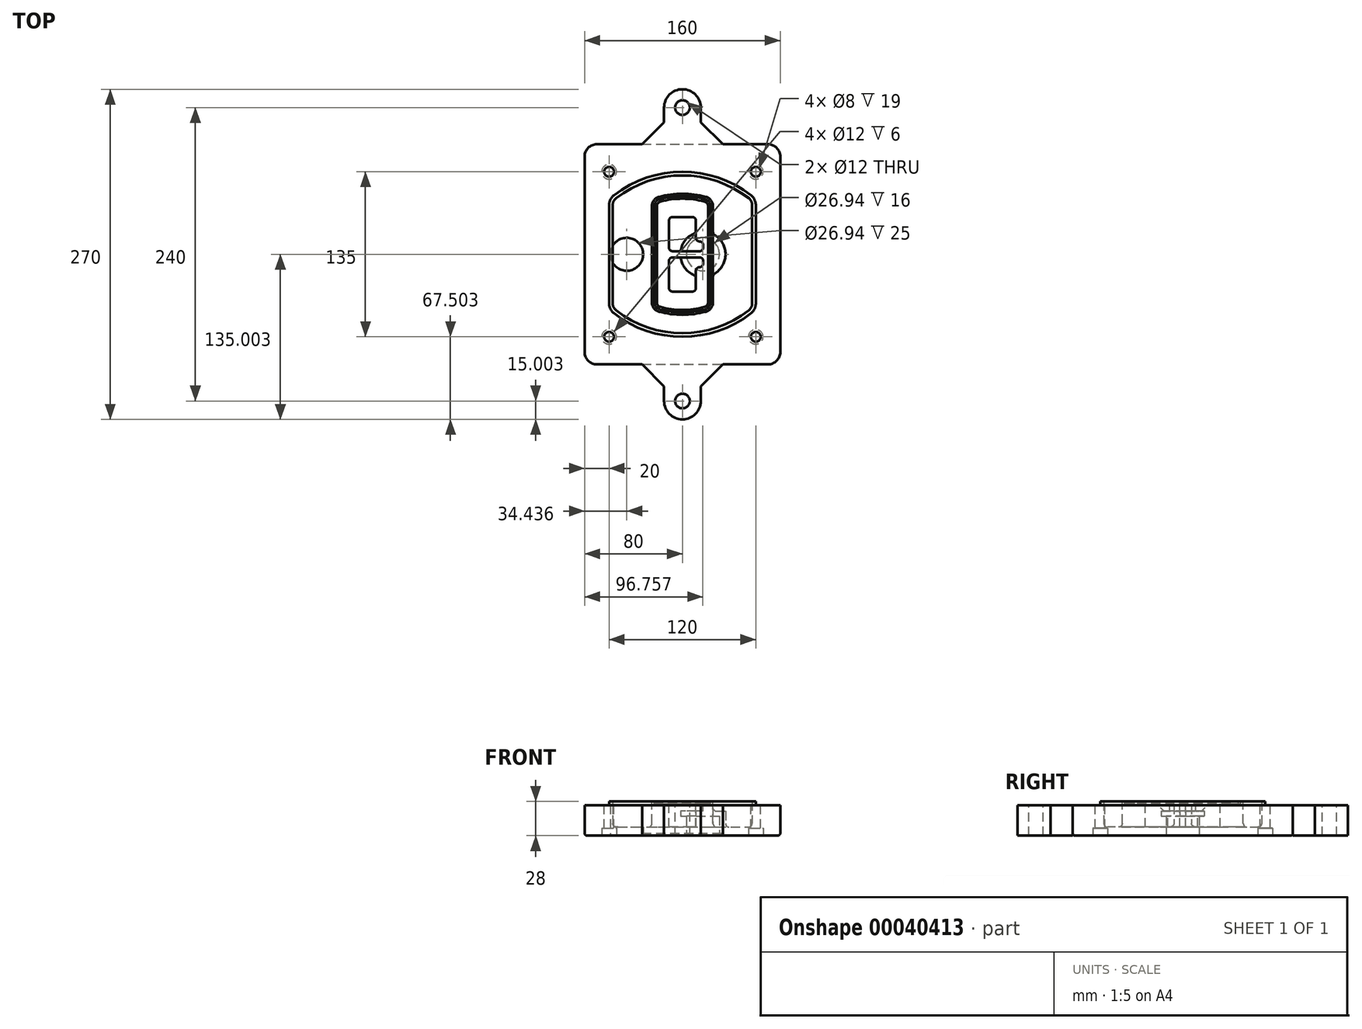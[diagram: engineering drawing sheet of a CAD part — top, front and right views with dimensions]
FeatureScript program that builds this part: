
annotation { "Feature Type Name" : "Feature", "Feature Type Description" : "" }
export const myFeature = defineFeature(function(context is Context, id is Id, definition is map)
    precondition{}
    {
        {
            var Q0;
            Q0=qCreatedBy(makeId("Top.planeOp"),FACE);
            var sketch = newSketch(context, id + "F0", { "sketchPlane" : qUnion([Q0])});
            skPoint(sketch, "E0.rect.middle", {"position": v(0, 0) * mm});
            skLineSegment(sketch, "E1.bottom", {"start": v(24.05, 28.38) * mm, "end": v(164.05, 28.38) * mm});
            skLineSegment(sketch, "E1.top", {"start": v(24.05, 208.38) * mm, "end": v(164.05, 208.38) * mm});
            skLineSegment(sketch, "E1.left", {"start": v(14.05, 38.38) * mm, "end": v(14.05, 198.38) * mm});
            skLineSegment(sketch, "E1.right", {"start": v(174.05, 38.38) * mm, "end": v(174.05, 198.38) * mm});
            skLineSegment(sketch, "E2", {"start": v(14.05, 208.38) * mm, "end": v(174.05, 28.38) * mm, "construction": true});
            skLineSegment(sketch, "E3", {"start": v(174.05, 208.38) * mm, "end": v(14.05, 28.38) * mm, "construction": true});
            skCircle(sketch, "E4", {"center": v(34.05, 185.88) * mm, "radius": 4 * mm});
            skCircle(sketch, "E5", {"center": v(154.05, 185.88) * mm, "radius": 4 * mm});
            skCircle(sketch, "E6", {"center": v(154.05, 50.88) * mm, "radius": 4 * mm});
            skCircle(sketch, "E7", {"center": v(34.05, 50.88) * mm, "radius": 4 * mm});
            skLineSegment(sketch, "E8", {"start": v(34.05, 185.88) * mm, "end": v(154.05, 185.88) * mm, "construction": true});
            skLineSegment(sketch, "E9", {"start": v(154.05, 185.88) * mm, "end": v(154.05, 50.88) * mm, "construction": true});
            skLineSegment(sketch, "E10", {"start": v(154.05, 50.88) * mm, "end": v(34.05, 50.88) * mm, "construction": true});
            skLineSegment(sketch, "E11", {"start": v(34.05, 50.88) * mm, "end": v(34.05, 185.88) * mm, "construction": true});
            skLineSegment(sketch, "E12", {"start": v(34.05, 158.68) * mm, "end": v(34.05, 78.09) * mm});
            skLineSegment(sketch, "E13", {"start": v(154.05, 158.68) * mm, "end": v(154.05, 78.09) * mm});
            skArc(sketch, "E14", {"start": v(150.2, 166.56) * mm, "mid": v(94.05, 185.88) * mm, "end": v(37.9, 166.56) * mm});
            skArc(sketch, "E15", {"start": v(37.9, 70.2) * mm, "mid": v(94.05, 50.88) * mm, "end": v(150.2, 70.2) * mm});
            skLineSegment(sketch, "E16", {"start": v(34.05, 118.38) * mm, "end": v(154.05, 118.38) * mm, "construction": true});
            skPoint(sketch, "E17.visualSharp", {"position": v(34.05, 73.38) * mm});
            skArc(sketch, "E17.filletArc", {"start": v(34.05, 78.09) * mm, "mid": v(35.06, 73.7) * mm, "end": v(37.9, 70.2) * mm});
            skPoint(sketch, "E18.visualSharp", {"position": v(34.05, 163.38) * mm});
            skArc(sketch, "E18.filletArc", {"start": v(37.9, 166.56) * mm, "mid": v(35.06, 163.06) * mm, "end": v(34.05, 158.68) * mm});
            skPoint(sketch, "E19.visualSharp", {"position": v(154.05, 163.38) * mm});
            skArc(sketch, "E19.filletArc", {"start": v(154.05, 158.68) * mm, "mid": v(153.04, 163.06) * mm, "end": v(150.2, 166.56) * mm});
            skPoint(sketch, "E20.visualSharp", {"position": v(154.05, 73.38) * mm});
            skArc(sketch, "E20.filletArc", {"start": v(150.2, 70.2) * mm, "mid": v(153.04, 73.7) * mm, "end": v(154.05, 78.09) * mm});
            skPoint(sketch, "E21.visualSharp", {"position": v(14.05, 208.38) * mm});
            skArc(sketch, "E21.filletArc", {"start": v(24.05, 208.38) * mm, "mid": v(16.98, 205.45) * mm, "end": v(14.05, 198.38) * mm});
            skPoint(sketch, "E22.visualSharp", {"position": v(174.05, 208.38) * mm});
            skArc(sketch, "E22.filletArc", {"start": v(174.05, 198.38) * mm, "mid": v(171.12, 205.45) * mm, "end": v(164.05, 208.38) * mm});
            skPoint(sketch, "E23.visualSharp", {"position": v(174.05, 28.38) * mm});
            skArc(sketch, "E23.filletArc", {"start": v(164.05, 28.38) * mm, "mid": v(171.12, 31.31) * mm, "end": v(174.05, 38.38) * mm});
            skPoint(sketch, "E24.visualSharp", {"position": v(14.05, 28.38) * mm});
            skArc(sketch, "E24.filletArc", {"start": v(14.05, 38.38) * mm, "mid": v(16.98, 31.31) * mm, "end": v(24.05, 28.38) * mm});
            skArc(sketch, "E25.0", {"start": v(151.05, 158.68) * mm, "mid": v(150.34, 161.75) * mm, "end": v(148.36, 164.2) * mm});
            skLineSegment(sketch, "E25.1", {"start": v(151.05, 158.68) * mm, "end": v(151.05, 78.09) * mm});
            skArc(sketch, "E25.2", {"start": v(148.36, 72.57) * mm, "mid": v(150.34, 75.02) * mm, "end": v(151.05, 78.09) * mm});
            skArc(sketch, "E25.3", {"start": v(39.74, 72.57) * mm, "mid": v(94.05, 53.88) * mm, "end": v(148.36, 72.57) * mm});
            skArc(sketch, "E25.4", {"start": v(37.05, 78.09) * mm, "mid": v(37.76, 75.02) * mm, "end": v(39.74, 72.57) * mm});
            skArc(sketch, "E25.5", {"start": v(148.36, 164.2) * mm, "mid": v(94.05, 182.88) * mm, "end": v(39.74, 164.2) * mm});
            skLineSegment(sketch, "E25.6", {"start": v(37.05, 158.68) * mm, "end": v(37.05, 78.09) * mm});
            skArc(sketch, "E25.7", {"start": v(39.74, 164.2) * mm, "mid": v(37.76, 161.75) * mm, "end": v(37.05, 158.68) * mm});
            skArc(sketch, "E26.0", {"start": v(35.43, 169.71) * mm, "mid": v(31.47, 164.82) * mm, "end": v(30.05, 158.68) * mm});
            skArc(sketch, "E26.1", {"start": v(152.67, 169.71) * mm, "mid": v(94.05, 189.88) * mm, "end": v(35.43, 169.71) * mm});
            skArc(sketch, "E26.2", {"start": v(158.05, 158.68) * mm, "mid": v(156.63, 164.82) * mm, "end": v(152.67, 169.71) * mm});
            skLineSegment(sketch, "E26.3", {"start": v(158.05, 158.68) * mm, "end": v(158.05, 78.09) * mm});
            skArc(sketch, "E26.4", {"start": v(152.67, 67.05) * mm, "mid": v(156.63, 71.95) * mm, "end": v(158.05, 78.09) * mm});
            skLineSegment(sketch, "E26.5", {"start": v(30.05, 158.68) * mm, "end": v(30.05, 78.09) * mm});
            skArc(sketch, "E26.6", {"start": v(35.43, 67.05) * mm, "mid": v(94.05, 46.88) * mm, "end": v(152.67, 67.05) * mm});
            skArc(sketch, "E26.7", {"start": v(30.05, 78.09) * mm, "mid": v(31.47, 71.95) * mm, "end": v(35.43, 67.05) * mm});
            skSolve(sketch);
        }
        {
            var Q0;
            Q0=makeQuery(id+"F0.imprint","IMPRINT",FACE,{"disambiguationData":[TD([[makeQuery(id+"F0.imprint","IMPRINT",EDGE,{"derivedFrom":sQuery(id+"F0.wireOp",EDGE,"E1.bottom")}),1.0]])]});
            var Q1;
            Q1=makeQuery(id+"F0.imprint","IMPRINT",FACE,{"disambiguationData":[TD([[makeQuery(id+"F0.imprint","IMPRINT",EDGE,{"derivedFrom":sQuery(id+"F0.wireOp",EDGE,"E12")}),1.0]])]});
            var Q2;
            Q2=makeQuery(id+"F0.imprint","IMPRINT",FACE,{"disambiguationData":[TD([[makeQuery(id+"F0.imprint","IMPRINT",EDGE,{"derivedFrom":sQuery(id+"F0.wireOp",EDGE,"E25.0")}),1.0]])]});
            var Q3;
            Q3=makeQuery(id+"F0.imprint","IMPRINT",FACE,{"disambiguationData":[TD([[makeQuery(id+"F0.imprint","IMPRINT",EDGE,{"derivedFrom":sQuery(id+"F0.wireOp",EDGE,"E12")}),-1.0]])]});
            extrude(context, id + "F1", {"entities" : qUnion([Q0, Q1, Q2, Q3]), "oppositeDirection" : true, "depth" : 25 * mm});
        }
        {
            var Q0;
            Q0=makeQuery(id+"F0.imprint","IMPRINT",FACE,{"disambiguationData":[TD([[makeQuery(id+"F0.imprint","IMPRINT",EDGE,{"derivedFrom":sQuery(id+"F0.wireOp",EDGE,"E12")}),1.0]])]});
            extrude(context, id + "F2", {"entities" : qUnion([Q0]), "operationType" : NewBodyOperationType.ADD, "depth" : 3 * mm});
        }
        {
            var Q0;
            Q0=makeQuery(id+"F0.imprint","IMPRINT",FACE,{"disambiguationData":[TD([[makeQuery(id+"F0.imprint","IMPRINT",EDGE,{"derivedFrom":sQuery(id+"F0.wireOp",EDGE,"E25.0")}),1.0]])]});
            extrude(context, id + "F3", {"entities" : qUnion([Q0]), "operationType" : NewBodyOperationType.REMOVE, "oppositeDirection" : true, "depth" : 18 * mm});
        }
        {
            var Q0;
            Q0=makeQuery(id+"F2.opExtrude","CAP_FACE",FACE,{"disambiguationData":[OSD([sQuery(id+"F0.wireOp",EDGE,"E12"),sQuery(id+"F0.wireOp",EDGE,"E13"),sQuery(id+"F0.wireOp",EDGE,"E14"),sQuery(id+"F0.wireOp",EDGE,"E15"),sQuery(id+"F0.wireOp",EDGE,"E17.filletArc"),sQuery(id+"F0.wireOp",EDGE,"E18.filletArc"),sQuery(id+"F0.wireOp",EDGE,"E19.filletArc"),sQuery(id+"F0.wireOp",EDGE,"E20.filletArc"),sQuery(id+"F0.wireOp",EDGE,"E25.0"),sQuery(id+"F0.wireOp",EDGE,"E25.1"),sQuery(id+"F0.wireOp",EDGE,"E25.2"),sQuery(id+"F0.wireOp",EDGE,"E25.3"),sQuery(id+"F0.wireOp",EDGE,"E25.4"),sQuery(id+"F0.wireOp",EDGE,"E25.5"),sQuery(id+"F0.wireOp",EDGE,"E25.6"),sQuery(id+"F0.wireOp",EDGE,"E25.7")])],"isStart":false});
            var sketch = newSketch(context, id + "F4", { "sketchPlane" : qUnion([Q0])});
            skArc(sketch, "E27.0", {"start": v(74.97, 71.41) * mm, "mid": v(94.05, 68.88) * mm, "end": v(113.13, 71.41) * mm});
            skArc(sketch, "E28.0", {"start": v(113.13, 165.35) * mm, "mid": v(94.05, 167.88) * mm, "end": v(74.97, 165.35) * mm});
            skLineSegment(sketch, "E29", {"start": v(69.05, 157.63) * mm, "end": v(69.05, 79.14) * mm});
            skLineSegment(sketch, "E30", {"start": v(119.05, 157.63) * mm, "end": v(119.05, 79.14) * mm});
            skLineSegment(sketch, "E31", {"start": v(69.05, 163.48) * mm, "end": v(119.05, 163.48) * mm, "construction": true});
            skLineSegment(sketch, "E32", {"start": v(69.05, 73.28) * mm, "end": v(119.05, 73.28) * mm, "construction": true});
            skPoint(sketch, "E33.visualSharp", {"position": v(69.05, 163.48) * mm});
            skArc(sketch, "E33.filletArc", {"start": v(74.97, 165.35) * mm, "mid": v(70.7, 162.5) * mm, "end": v(69.05, 157.63) * mm});
            skPoint(sketch, "E34.visualSharp", {"position": v(119.05, 163.48) * mm});
            skArc(sketch, "E34.filletArc", {"start": v(119.05, 157.63) * mm, "mid": v(117.4, 162.5) * mm, "end": v(113.13, 165.35) * mm});
            skPoint(sketch, "E35.visualSharp", {"position": v(119.05, 73.28) * mm});
            skArc(sketch, "E35.filletArc", {"start": v(113.13, 71.41) * mm, "mid": v(117.4, 74.27) * mm, "end": v(119.05, 79.14) * mm});
            skPoint(sketch, "E36.visualSharp", {"position": v(69.05, 73.28) * mm});
            skArc(sketch, "E36.filletArc", {"start": v(69.05, 79.14) * mm, "mid": v(70.7, 74.27) * mm, "end": v(74.97, 71.41) * mm});
            skArc(sketch, "E37.0", {"start": v(148.36, 164.2) * mm, "mid": v(94.05, 182.88) * mm, "end": v(39.74, 164.2) * mm});
            skArc(sketch, "E37.1", {"start": v(39.74, 164.2) * mm, "mid": v(37.76, 161.75) * mm, "end": v(37.05, 158.68) * mm});
            skLineSegment(sketch, "E37.2", {"start": v(37.05, 158.68) * mm, "end": v(37.05, 78.09) * mm});
            skArc(sketch, "E37.3", {"start": v(37.05, 78.09) * mm, "mid": v(37.76, 75.02) * mm, "end": v(39.74, 72.57) * mm});
            skArc(sketch, "E37.4", {"start": v(39.74, 72.57) * mm, "mid": v(94.05, 53.88) * mm, "end": v(148.36, 72.57) * mm});
            skArc(sketch, "E37.5", {"start": v(148.36, 72.57) * mm, "mid": v(150.34, 75.02) * mm, "end": v(151.05, 78.09) * mm});
            skLineSegment(sketch, "E37.6", {"start": v(151.05, 158.68) * mm, "end": v(151.05, 78.09) * mm});
            skArc(sketch, "E37.7", {"start": v(151.05, 158.68) * mm, "mid": v(150.34, 161.75) * mm, "end": v(148.36, 164.2) * mm});
            skLineSegment(sketch, "E38.0", {"start": v(117.05, 157.63) * mm, "end": v(117.05, 79.14) * mm});
            skArc(sketch, "E38.1", {"start": v(112.61, 73.34) * mm, "mid": v(115.81, 75.49) * mm, "end": v(117.05, 79.14) * mm});
            skArc(sketch, "E38.2", {"start": v(75.49, 73.34) * mm, "mid": v(94.05, 70.88) * mm, "end": v(112.61, 73.34) * mm});
            skArc(sketch, "E38.3", {"start": v(71.05, 79.14) * mm, "mid": v(72.29, 75.49) * mm, "end": v(75.49, 73.34) * mm});
            skLineSegment(sketch, "E38.4", {"start": v(71.05, 157.63) * mm, "end": v(71.05, 79.14) * mm});
            skArc(sketch, "E38.5", {"start": v(117.05, 157.63) * mm, "mid": v(115.81, 161.28) * mm, "end": v(112.61, 163.42) * mm});
            skArc(sketch, "E38.6", {"start": v(75.49, 163.42) * mm, "mid": v(72.29, 161.28) * mm, "end": v(71.05, 157.63) * mm});
            skArc(sketch, "E38.7", {"start": v(112.61, 163.42) * mm, "mid": v(94.05, 165.88) * mm, "end": v(75.49, 163.42) * mm});
            skArc(sketch, "E39.0", {"start": v(115.05, 157.63) * mm, "mid": v(114.23, 160.06) * mm, "end": v(112.1, 161.5) * mm});
            skLineSegment(sketch, "E39.1", {"start": v(115.05, 157.63) * mm, "end": v(115.05, 79.14) * mm});
            skArc(sketch, "E39.2", {"start": v(112.1, 75.27) * mm, "mid": v(114.23, 76.7) * mm, "end": v(115.05, 79.14) * mm});
            skArc(sketch, "E39.3", {"start": v(76, 75.27) * mm, "mid": v(94.05, 72.88) * mm, "end": v(112.1, 75.27) * mm});
            skArc(sketch, "E39.4", {"start": v(73.05, 79.14) * mm, "mid": v(73.87, 76.7) * mm, "end": v(76, 75.27) * mm});
            skArc(sketch, "E39.5", {"start": v(112.1, 161.5) * mm, "mid": v(94.05, 163.88) * mm, "end": v(76, 161.5) * mm});
            skLineSegment(sketch, "E39.6", {"start": v(73.05, 157.63) * mm, "end": v(73.05, 79.14) * mm});
            skArc(sketch, "E39.7", {"start": v(76, 161.5) * mm, "mid": v(73.87, 160.06) * mm, "end": v(73.05, 157.63) * mm});
            skLineSegment(sketch, "E40", {"start": v(69.05, 118.38) * mm, "end": v(119.05, 118.38) * mm, "construction": true});
            skLineSegment(sketch, "E41", {"start": v(83.05, 123.88) * mm, "end": v(83.05, 145.88) * mm});
            skLineSegment(sketch, "E42", {"start": v(86.05, 148.88) * mm, "end": v(102.05, 148.88) * mm});
            skLineSegment(sketch, "E43", {"start": v(105.05, 145.88) * mm, "end": v(105.05, 131.88) * mm});
            skLineSegment(sketch, "E44", {"start": v(108.05, 128.88) * mm, "end": v(108.05, 128.88) * mm});
            skLineSegment(sketch, "E45", {"start": v(111.05, 125.88) * mm, "end": v(111.05, 123.88) * mm});
            skLineSegment(sketch, "E46", {"start": v(108.05, 120.88) * mm, "end": v(86.05, 120.88) * mm});
            skPoint(sketch, "E47.visualSharp", {"position": v(83.05, 148.88) * mm});
            skArc(sketch, "E47.filletArc", {"start": v(86.05, 148.88) * mm, "mid": v(83.93, 148) * mm, "end": v(83.05, 145.88) * mm});
            skPoint(sketch, "E48.visualSharp", {"position": v(105.05, 148.88) * mm});
            skArc(sketch, "E48.filletArc", {"start": v(105.05, 145.88) * mm, "mid": v(104.17, 148) * mm, "end": v(102.05, 148.88) * mm});
            skPoint(sketch, "E49.visualSharp", {"position": v(105.05, 128.88) * mm});
            skArc(sketch, "E49.filletArc", {"start": v(105.05, 131.88) * mm, "mid": v(105.93, 129.76) * mm, "end": v(108.05, 128.88) * mm});
            skPoint(sketch, "E50.visualSharp", {"position": v(111.05, 128.88) * mm});
            skArc(sketch, "E50.filletArc", {"start": v(111.05, 125.88) * mm, "mid": v(110.17, 128) * mm, "end": v(108.05, 128.88) * mm});
            skPoint(sketch, "E51.visualSharp", {"position": v(111.05, 120.88) * mm});
            skArc(sketch, "E51.filletArc", {"start": v(108.05, 120.88) * mm, "mid": v(110.17, 121.76) * mm, "end": v(111.05, 123.88) * mm});
            skPoint(sketch, "E52.visualSharp", {"position": v(83.05, 120.88) * mm});
            skArc(sketch, "E52.filletArc", {"start": v(83.05, 123.88) * mm, "mid": v(83.93, 121.76) * mm, "end": v(86.05, 120.88) * mm});
            skLineSegment(sketch, "E53.0.MirrorCS", {"start": v(108.05, 115.88) * mm, "end": v(86.05, 115.88) * mm});
            skArc(sketch, "E54.0.MirrorCS", {"start": v(83.05, 112.88) * mm, "mid": v(83.93, 115) * mm, "end": v(86.05, 115.88) * mm});
            skLineSegment(sketch, "E55.0.MirrorCS", {"start": v(83.05, 112.88) * mm, "end": v(83.05, 90.88) * mm});
            skArc(sketch, "E56.0.MirrorCS", {"start": v(86.05, 87.88) * mm, "mid": v(83.93, 88.76) * mm, "end": v(83.05, 90.88) * mm});
            skLineSegment(sketch, "E57.0.MirrorCS", {"start": v(86.05, 87.88) * mm, "end": v(102.05, 87.88) * mm});
            skArc(sketch, "E58.0.MirrorCS", {"start": v(105.05, 90.88) * mm, "mid": v(104.17, 88.76) * mm, "end": v(102.05, 87.88) * mm});
            skLineSegment(sketch, "E59.0.MirrorCS", {"start": v(105.05, 90.88) * mm, "end": v(105.05, 104.88) * mm});
            skArc(sketch, "E60.0.MirrorCS", {"start": v(105.05, 104.88) * mm, "mid": v(105.93, 107) * mm, "end": v(108.05, 107.88) * mm});
            skArc(sketch, "E61.0.MirrorCS", {"start": v(111.05, 110.88) * mm, "mid": v(110.17, 108.76) * mm, "end": v(108.05, 107.88) * mm});
            skLineSegment(sketch, "E62.0.MirrorCS", {"start": v(111.05, 110.88) * mm, "end": v(111.05, 112.88) * mm});
            skArc(sketch, "E63.0.MirrorCS", {"start": v(108.05, 115.88) * mm, "mid": v(110.17, 115) * mm, "end": v(111.05, 112.88) * mm});
            skSolve(sketch);
        }
        {
            var Q0;
            Q0=makeQuery(id+"F4.imprint","IMPRINT",FACE,{"disambiguationData":[TD([[makeQuery(id+"F4.imprint","IMPRINT",EDGE,{"derivedFrom":sQuery(id+"F4.wireOp",EDGE,"E27.0")}),1.0]])]});
            var Q1;
            Q1=makeQuery(id+"F4.imprint","IMPRINT",FACE,{"disambiguationData":[TD([[makeQuery(id+"F4.imprint","IMPRINT",EDGE,{"derivedFrom":sQuery(id+"F4.wireOp",EDGE,"E38.0")}),-1.0]])]});
            var Q2;
            Q2=makeQuery(id+"F4.imprint","IMPRINT",FACE,{"disambiguationData":[TD([[makeQuery(id+"F4.imprint","IMPRINT",EDGE,{"derivedFrom":sQuery(id+"F4.wireOp",EDGE,"E39.0")}),1.0]])]});
            extrude(context, id + "F5", {"entities" : qUnion([Q0, Q1, Q2]), "operationType" : NewBodyOperationType.ADD, "endBound" : BoundingType.UP_TO_NEXT, "oppositeDirection" : true, "depth" : 25 * mm});
        }
        {
            var Q0;
            Q0=makeQuery(id+"F4.imprint","IMPRINT",FACE,{"disambiguationData":[TD([[makeQuery(id+"F4.imprint","IMPRINT",EDGE,{"derivedFrom":sQuery(id+"F4.wireOp",EDGE,"E38.0")}),-1.0]])]});
            extrude(context, id + "F6", {"entities" : qUnion([Q0]), "operationType" : NewBodyOperationType.REMOVE, "oppositeDirection" : true, "depth" : 2 * mm});
        }
        {
            var Q0;
            Q0=makeQuery(id+"F1.opExtrude","CAP_FACE",FACE,{"disambiguationData":[OSD([sQuery(id+"F0.wireOp",EDGE,"E1.bottom"),sQuery(id+"F0.wireOp",EDGE,"E1.top"),sQuery(id+"F0.wireOp",EDGE,"E1.left"),sQuery(id+"F0.wireOp",EDGE,"E1.right"),sQuery(id+"F0.wireOp",EDGE,"E4"),sQuery(id+"F0.wireOp",EDGE,"E5"),sQuery(id+"F0.wireOp",EDGE,"E6"),sQuery(id+"F0.wireOp",EDGE,"E7"),sQuery(id+"F0.wireOp",EDGE,"E21.filletArc"),sQuery(id+"F0.wireOp",EDGE,"E22.filletArc"),sQuery(id+"F0.wireOp",EDGE,"E23.filletArc"),sQuery(id+"F0.wireOp",EDGE,"E24.filletArc")])],"isStart":false});
            var sketch = newSketch(context, id + "F7", { "sketchPlane" : qUnion([Q0])});
            skCircle(sketch, "E64", {"center": v(110.8, -118.38) * mm, "radius": 13.47 * mm});
            skCircle(sketch, "E65", {"center": v(48.49, -118.38) * mm, "radius": 13.47 * mm});
            skLineSegment(sketch, "E66", {"start": v(174.05, -118.38) * mm, "end": v(14.05, -118.38) * mm});
            skCircle(sketch, "E67", {"center": v(110.8, -118.38) * mm, "radius": 18.47 * mm});
            skCircle(sketch, "E68", {"center": v(154.05, -185.88) * mm, "radius": 6 * mm});
            skCircle(sketch, "E69", {"center": v(34.05, -185.88) * mm, "radius": 6 * mm});
            skCircle(sketch, "E70", {"center": v(34.05, -50.88) * mm, "radius": 6 * mm});
            skCircle(sketch, "E71", {"center": v(154.05, -50.88) * mm, "radius": 6 * mm});
            skSolve(sketch);
        }
        {
            var Q0;
            {var subQ1=sQuery(id+"F7.wireOp",EDGE,"E66");var subQ4=sQuery(id+"F7.wireOp",EDGE,"E64");var subQ6=makeQuery(id+"F7.imprint","INTERSECT",VERTEX,{"disambiguationData":[OD(0.0)],"derivedFrom":[subQ4,subQ1]});Q0=makeQuery(id+"F7.imprint","IMPRINT",FACE,{"disambiguationData":[TD([[makeQuery(id+"F7.imprint","IMPRINT",EDGE,{"disambiguationData":[TD([[subQ6,-1.0]])],"derivedFrom":subQ4}),-1.0]])]});}
            var Q1;
            {var subQ0=sQuery(id+"F7.wireOp",EDGE,"E66");var subQ1=sQuery(id+"F7.wireOp",EDGE,"E64");var subQ3=makeQuery(id+"F7.imprint","INTERSECT",VERTEX,{"disambiguationData":[OD(0.0)],"derivedFrom":[subQ1,subQ0]});Q1=makeQuery(id+"F7.imprint","IMPRINT",FACE,{"disambiguationData":[TD([[makeQuery(id+"F7.imprint","IMPRINT",EDGE,{"disambiguationData":[TD([[subQ3,-1.0]])],"derivedFrom":subQ1}),1.0]])]});}
            var Q2;
            {var subQ0=sQuery(id+"F7.wireOp",EDGE,"E66");var subQ1=sQuery(id+"F7.wireOp",EDGE,"E64");var subQ3=makeQuery(id+"F7.imprint","INTERSECT",VERTEX,{"disambiguationData":[OD(0.0)],"derivedFrom":[subQ1,subQ0]});Q2=makeQuery(id+"F7.imprint","IMPRINT",FACE,{"disambiguationData":[TD([[makeQuery(id+"F7.imprint","IMPRINT",EDGE,{"disambiguationData":[TD([[subQ3,1.0]])],"derivedFrom":subQ1}),1.0]])]});}
            var Q3;
            {var subQ1=sQuery(id+"F7.wireOp",EDGE,"E66");var subQ4=sQuery(id+"F7.wireOp",EDGE,"E64");var subQ6=makeQuery(id+"F7.imprint","INTERSECT",VERTEX,{"disambiguationData":[OD(0.0)],"derivedFrom":[subQ4,subQ1]});Q3=makeQuery(id+"F7.imprint","IMPRINT",FACE,{"disambiguationData":[TD([[makeQuery(id+"F7.imprint","IMPRINT",EDGE,{"disambiguationData":[TD([[subQ6,1.0]])],"derivedFrom":subQ4}),-1.0]])]});}
            extrude(context, id + "F8", {"entities" : qUnion([Q0, Q1, Q2, Q3]), "operationType" : NewBodyOperationType.ADD, "oppositeDirection" : true, "depth" : 20 * mm});
        }
        {
            var Q0;
            {var subQ0=sQuery(id+"F7.wireOp",EDGE,"E66");var subQ1=sQuery(id+"F7.wireOp",EDGE,"E64");var subQ3=makeQuery(id+"F7.imprint","INTERSECT",VERTEX,{"disambiguationData":[OD(0.0)],"derivedFrom":[subQ1,subQ0]});Q0=makeQuery(id+"F7.imprint","IMPRINT",FACE,{"disambiguationData":[TD([[makeQuery(id+"F7.imprint","IMPRINT",EDGE,{"disambiguationData":[TD([[subQ3,-1.0]])],"derivedFrom":subQ1}),1.0]])]});}
            var Q1;
            {var subQ0=sQuery(id+"F7.wireOp",EDGE,"E66");var subQ1=sQuery(id+"F7.wireOp",EDGE,"E64");var subQ3=makeQuery(id+"F7.imprint","INTERSECT",VERTEX,{"disambiguationData":[OD(0.0)],"derivedFrom":[subQ1,subQ0]});Q1=makeQuery(id+"F7.imprint","IMPRINT",FACE,{"disambiguationData":[TD([[makeQuery(id+"F7.imprint","IMPRINT",EDGE,{"disambiguationData":[TD([[subQ3,1.0]])],"derivedFrom":subQ1}),1.0]])]});}
            extrude(context, id + "F9", {"entities" : qUnion([Q0, Q1]), "operationType" : NewBodyOperationType.REMOVE, "oppositeDirection" : true, "depth" : 16 * mm});
        }
        {
            var Q0;
            {var subQ0=sQuery(id+"F7.wireOp",EDGE,"E66");var subQ1=sQuery(id+"F7.wireOp",EDGE,"E65");var subQ3=makeQuery(id+"F7.imprint","INTERSECT",VERTEX,{"disambiguationData":[OD(0.0)],"derivedFrom":[subQ1,subQ0]});Q0=makeQuery(id+"F7.imprint","IMPRINT",FACE,{"disambiguationData":[TD([[makeQuery(id+"F7.imprint","IMPRINT",EDGE,{"disambiguationData":[TD([[subQ3,-1.0]])],"derivedFrom":subQ1}),1.0]])]});}
            var Q1;
            {var subQ0=sQuery(id+"F7.wireOp",EDGE,"E66");var subQ1=sQuery(id+"F7.wireOp",EDGE,"E65");var subQ3=makeQuery(id+"F7.imprint","INTERSECT",VERTEX,{"disambiguationData":[OD(0.0)],"derivedFrom":[subQ1,subQ0]});Q1=makeQuery(id+"F7.imprint","IMPRINT",FACE,{"disambiguationData":[TD([[makeQuery(id+"F7.imprint","IMPRINT",EDGE,{"disambiguationData":[TD([[subQ3,1.0]])],"derivedFrom":subQ1}),1.0]])]});}
            extrude(context, id + "F10", {"entities" : qUnion([Q0, Q1]), "operationType" : NewBodyOperationType.REMOVE, "oppositeDirection" : true, "depth" : 25 * mm});
        }
        {
            var Q0;
            Q0=makeQuery(id+"F7.imprint","IMPRINT",FACE,{"disambiguationData":[TD([[makeQuery(id+"F7.imprint","IMPRINT",EDGE,{"derivedFrom":sQuery(id+"F7.wireOp",EDGE,"E68")}),1.0]])]});
            var Q1;
            Q1=makeQuery(id+"F7.imprint","IMPRINT",FACE,{"disambiguationData":[TD([[makeQuery(id+"F7.imprint","IMPRINT",EDGE,{"derivedFrom":makeQuery(id+"F1.opExtrude","CAP_EDGE",EDGE,{"disambiguationData":[OSD([sQuery(id+"F0.wireOp",EDGE,"E5")])],"isStart":false})}),-1.0]])]});
            var Q2;
            Q2=makeQuery(id+"F7.imprint","IMPRINT",FACE,{"disambiguationData":[TD([[makeQuery(id+"F7.imprint","IMPRINT",EDGE,{"derivedFrom":sQuery(id+"F7.wireOp",EDGE,"E69")}),1.0]])]});
            var Q3;
            Q3=makeQuery(id+"F7.imprint","IMPRINT",FACE,{"disambiguationData":[TD([[makeQuery(id+"F7.imprint","IMPRINT",EDGE,{"derivedFrom":makeQuery(id+"F1.opExtrude","CAP_EDGE",EDGE,{"disambiguationData":[OSD([sQuery(id+"F0.wireOp",EDGE,"E4")])],"isStart":false})}),-1.0]])]});
            var Q4;
            Q4=makeQuery(id+"F7.imprint","IMPRINT",FACE,{"disambiguationData":[TD([[makeQuery(id+"F7.imprint","IMPRINT",EDGE,{"derivedFrom":sQuery(id+"F7.wireOp",EDGE,"E70")}),1.0]])]});
            var Q5;
            Q5=makeQuery(id+"F7.imprint","IMPRINT",FACE,{"disambiguationData":[TD([[makeQuery(id+"F7.imprint","IMPRINT",EDGE,{"derivedFrom":makeQuery(id+"F1.opExtrude","CAP_EDGE",EDGE,{"disambiguationData":[OSD([sQuery(id+"F0.wireOp",EDGE,"E7")])],"isStart":false})}),-1.0]])]});
            var Q6;
            Q6=makeQuery(id+"F7.imprint","IMPRINT",FACE,{"disambiguationData":[TD([[makeQuery(id+"F7.imprint","IMPRINT",EDGE,{"derivedFrom":sQuery(id+"F7.wireOp",EDGE,"E71")}),1.0]])]});
            var Q7;
            Q7=makeQuery(id+"F7.imprint","IMPRINT",FACE,{"disambiguationData":[TD([[makeQuery(id+"F7.imprint","IMPRINT",EDGE,{"derivedFrom":makeQuery(id+"F1.opExtrude","CAP_EDGE",EDGE,{"disambiguationData":[OSD([sQuery(id+"F0.wireOp",EDGE,"E6")])],"isStart":false})}),-1.0]])]});
            extrude(context, id + "F11", {"entities" : qUnion([Q0, Q1, Q2, Q3, Q4, Q5, Q6, Q7]), "operationType" : NewBodyOperationType.REMOVE, "oppositeDirection" : true, "depth" : 6 * mm});
        }
        {
            var Q0;
            Q0=makeQuery(id+"F9.boolean.opBoolean","COPY",FACE,{"derivedFrom":makeQuery(id+"F9.opExtrude","CAP_FACE",FACE,{"disambiguationData":[OSD([sQuery(id+"F7.wireOp",EDGE,"E64")])],"isStart":false})});
            var sketch = newSketch(context, id + "F12", { "sketchPlane" : qUnion([Q0])});
            skArc(sketch, "E72.0", {"start": v(105.05, -100.83) * mm, "mid": v(96.62, -106.56) * mm, "end": v(92.5, -115.88) * mm});
            skArc(sketch, "E72.1", {"start": v(92.5, -120.88) * mm, "mid": v(96.62, -130.2) * mm, "end": v(105.05, -135.93) * mm});
            skLineSegment(sketch, "E73", {"start": v(92.5, -120.88) * mm, "end": v(108.05, -120.88) * mm});
            skLineSegment(sketch, "E74.0", {"start": v(108.05, -115.88) * mm, "end": v(92.5, -115.88) * mm});
            skArc(sketch, "E74.1", {"start": v(108.05, -115.88) * mm, "mid": v(110.17, -115) * mm, "end": v(111.05, -112.88) * mm});
            skLineSegment(sketch, "E74.2", {"start": v(111.05, -110.88) * mm, "end": v(111.05, -112.88) * mm});
            skArc(sketch, "E74.3", {"start": v(111.05, -110.88) * mm, "mid": v(110.17, -108.76) * mm, "end": v(108.05, -107.88) * mm});
            skArc(sketch, "E74.4", {"start": v(105.05, -104.88) * mm, "mid": v(105.93, -107) * mm, "end": v(108.05, -107.88) * mm});
            skLineSegment(sketch, "E74.5", {"start": v(105.05, -100.83) * mm, "end": v(105.05, -104.88) * mm});
            skLineSegment(sketch, "E74.7", {"start": v(108.05, -120.88) * mm, "end": v(92.5, -120.88) * mm});
            skArc(sketch, "E74.8", {"start": v(108.05, -120.88) * mm, "mid": v(110.17, -121.76) * mm, "end": v(111.05, -123.88) * mm});
            skLineSegment(sketch, "E74.9", {"start": v(111.05, -125.88) * mm, "end": v(111.05, -123.88) * mm});
            skArc(sketch, "E74.10", {"start": v(111.05, -125.88) * mm, "mid": v(110.17, -128) * mm, "end": v(108.05, -128.88) * mm});
            skArc(sketch, "E74.11", {"start": v(105.05, -131.88) * mm, "mid": v(105.93, -129.76) * mm, "end": v(108.05, -128.88) * mm});
            skLineSegment(sketch, "E74.12", {"start": v(105.05, -135.93) * mm, "end": v(105.05, -131.88) * mm});
            skPoint(sketch, "E75.orphan", {"position": v(105.05, -145.88) * mm});
            skPoint(sketch, "E76.orphan", {"position": v(86.05, -120.88) * mm});
            skPoint(sketch, "E77.orphan", {"position": v(86.05, -115.88) * mm});
            skPoint(sketch, "E78.orphan", {"position": v(105.05, -90.88) * mm});
            skSolve(sketch);
        }
        {
            var Q0;
            {var subQ7=sQuery(id+"F12.wireOp",EDGE,"E72.0");var subQ14=sQuery(id+"F12.wireOp",EDGE,"E72.1");var subQ16=sQuery(id+"F12.wireOp",EDGE,"E74.1");var subQ18=sQuery(id+"F12.wireOp",EDGE,"E74.8");Q0=qUnion([makeQuery(id+"F12.imprint","IMPRINT",FACE,{"disambiguationData":[TD([[makeQuery(id+"F12.imprint","IMPRINT",EDGE,{"derivedFrom":subQ7}),1.0]])]}),makeQuery(id+"F12.imprint","IMPRINT",FACE,{"disambiguationData":[TD([[makeQuery(id+"F12.imprint","IMPRINT",EDGE,{"derivedFrom":subQ14}),1.0]])]}),makeQuery(id+"F12.imprint","IMPRINT",FACE,{"disambiguationData":[TD([[makeQuery(id+"F12.imprint","IMPRINT",EDGE,{"derivedFrom":subQ16}),1.0]])]}),makeQuery(id+"F12.imprint","IMPRINT",FACE,{"disambiguationData":[TD([[makeQuery(id+"F12.imprint","IMPRINT",EDGE,{"derivedFrom":subQ18}),-1.0]])]})]);}
            var Q1;
            Q1=makeQuery(id+"F5.boolean.opBoolean","SPLIT",FACE,{"disambiguationData":[TD([makeQuery(id+"F5.opExtrude","SWEPT_FACE",FACE,{"disambiguationData":[OSD([sQuery(id+"F4.wireOp",EDGE,"E41")])]})])],"derivedFrom":makeQuery(id+"F3.boolean.opBoolean","COPY",FACE,{"derivedFrom":makeQuery(id+"F3.opExtrude","CAP_FACE",FACE,{"disambiguationData":[OSD([sQuery(id+"F0.wireOp",EDGE,"E25.0"),sQuery(id+"F0.wireOp",EDGE,"E25.1"),sQuery(id+"F0.wireOp",EDGE,"E25.2"),sQuery(id+"F0.wireOp",EDGE,"E25.3"),sQuery(id+"F0.wireOp",EDGE,"E25.4"),sQuery(id+"F0.wireOp",EDGE,"E25.5"),sQuery(id+"F0.wireOp",EDGE,"E25.6"),sQuery(id+"F0.wireOp",EDGE,"E25.7")])],"isStart":false})})});
            extrude(context, id + "F13", {"entities" : qUnion([Q0]), "operationType" : NewBodyOperationType.REMOVE, "endBound" : BoundingType.UP_TO_SURFACE, "endBoundEntityFace" : qUnion([Q1]), "depth" : 25 * mm});
        }
        {
            var Q0;
            Q0=makeQuery(id+"F3.boolean.opBoolean","COPY",EDGE,{"derivedFrom":makeQuery(id+"F3.opExtrude","CAP_EDGE",EDGE,{"disambiguationData":[OSD([sQuery(id+"F0.wireOp",EDGE,"E25.6")])],"isStart":false})});
            var Q1;
            Q1=makeQuery(id+"F8.boolean.opBoolean","INTERSECT",EDGE,{"derivedFrom":[makeQuery(id+"F5.opExtrude","SWEPT_FACE",FACE,{"disambiguationData":[OSD([sQuery(id+"F4.wireOp",EDGE,"E30")])]}),makeQuery(id+"F8.opExtrude","CAP_FACE",FACE,{"disambiguationData":[OSD([sQuery(id+"F7.wireOp",EDGE,"E67")])],"isStart":false})]});
            var Q2;
            Q2=makeQuery(id+"F8.boolean.opBoolean","INTERSECT",EDGE,{"disambiguationData":[OD(1.0)],"derivedFrom":[makeQuery(id+"F5.opExtrude","SWEPT_FACE",FACE,{"disambiguationData":[OSD([sQuery(id+"F4.wireOp",EDGE,"E30")])]}),makeQuery(id+"F8.opExtrude","SWEPT_FACE",FACE,{"disambiguationData":[OSD([sQuery(id+"F7.wireOp",EDGE,"E67")])]})]});
            var Q3;
            {var subQ0=sQuery(id+"F4.wireOp",EDGE,"E30");Q3=makeQuery(id+"F8.boolean.opBoolean","SPLIT",EDGE,{"disambiguationData":[TD([makeQuery(id+"F5.opExtrude","SWEPT_FACE",FACE,{"disambiguationData":[OSD([sQuery(id+"F4.wireOp",EDGE,"E35.filletArc")])]})])],"derivedFrom":makeQuery(id+"F5.opExtrude","CAP_EDGE",EDGE,{"disambiguationData":[OSD([subQ0])],"isStart":false})});}
            var Q4;
            {var subQ0=sQuery(id+"F0.wireOp",EDGE,"E25.7");var subQ1=sQuery(id+"F0.wireOp",EDGE,"E25.1");var subQ2=sQuery(id+"F0.wireOp",EDGE,"E25.6");var subQ3=sQuery(id+"F0.wireOp",EDGE,"E25.5");var subQ4=sQuery(id+"F0.wireOp",EDGE,"E25.4");var subQ5=sQuery(id+"F0.wireOp",EDGE,"E25.0");var subQ6=sQuery(id+"F0.wireOp",EDGE,"E25.2");var subQ7=sQuery(id+"F0.wireOp",EDGE,"E25.3");Q4=makeQuery(id+"F8.boolean.opBoolean","INTERSECT",EDGE,{"derivedFrom":[makeQuery(id+"F5.boolean.opBoolean","SPLIT",FACE,{"disambiguationData":[TD([makeQuery(id+"F2.opExtrude","SWEPT_FACE",FACE,{"disambiguationData":[OSD([subQ5])]})])],"derivedFrom":makeQuery(id+"F3.boolean.opBoolean","COPY",FACE,{"derivedFrom":makeQuery(id+"F3.opExtrude","CAP_FACE",FACE,{"disambiguationData":[OSD([subQ5,subQ1,subQ6,subQ7,subQ4,subQ3,subQ2,subQ0])],"isStart":false})})}),makeQuery(id+"F8.opExtrude","SWEPT_FACE",FACE,{"disambiguationData":[OSD([sQuery(id+"F7.wireOp",EDGE,"E67")])]})]});}
            var Q5;
            Q5=makeQuery(id+"F8.boolean.opBoolean","INTERSECT",EDGE,{"disambiguationData":[OD(0.0)],"derivedFrom":[makeQuery(id+"F5.opExtrude","SWEPT_FACE",FACE,{"disambiguationData":[OSD([sQuery(id+"F4.wireOp",EDGE,"E30")])]}),makeQuery(id+"F8.opExtrude","SWEPT_FACE",FACE,{"disambiguationData":[OSD([sQuery(id+"F7.wireOp",EDGE,"E67")])]})]});
            fillet(context, id + "F14", {"entities" : qUnion([Q0, Q1, Q2, Q3, Q4, Q5]), "radius" : 3 * mm, "tangentPropagation" : true, "allowEdgeOverflow" : false});
        }
        {
            var Q0;
            Q0=makeQuery(id+"F1.opExtrude","CAP_EDGE",EDGE,{"disambiguationData":[OSD([sQuery(id+"F0.wireOp",EDGE,"E1.bottom")])],"isStart":false});
            fillet(context, id + "F15", {"entities" : qUnion([Q0]), "radius" : 2 * mm, "tangentPropagation" : true, "allowEdgeOverflow" : false});
        }
        {
            var Q0;
            {var subQ0=sQuery(id+"F0.wireOp",EDGE,"E1.bottom");var subQ1=sQuery(id+"F0.wireOp",EDGE,"E1.top");var subQ2=sQuery(id+"F0.wireOp",EDGE,"E1.left");var subQ3=sQuery(id+"F0.wireOp",EDGE,"E1.right");var subQ4=sQuery(id+"F0.wireOp",EDGE,"E4");var subQ5=sQuery(id+"F0.wireOp",EDGE,"E5");var subQ6=sQuery(id+"F0.wireOp",EDGE,"E6");var subQ7=sQuery(id+"F0.wireOp",EDGE,"E7");var subQ8=sQuery(id+"F0.wireOp",EDGE,"E21.filletArc");var subQ9=sQuery(id+"F0.wireOp",EDGE,"E22.filletArc");var subQ10=sQuery(id+"F0.wireOp",EDGE,"E23.filletArc");var subQ11=sQuery(id+"F0.wireOp",EDGE,"E24.filletArc");Q0=makeQuery(id+"F2.boolean.opBoolean","SPLIT",FACE,{"disambiguationData":[TD([makeQuery(id+"F1.opExtrude","SWEPT_FACE",FACE,{"disambiguationData":[OSD([subQ0])]})])],"derivedFrom":makeQuery(id+"F1.opExtrude","CAP_FACE",FACE,{"disambiguationData":[OSD([subQ0,subQ1,subQ2,subQ3,subQ4,subQ5,subQ6,subQ7,subQ8,subQ9,subQ10,subQ11])],"isStart":true})});}
            var sketch = newSketch(context, id + "F16", { "sketchPlane" : qUnion([Q0])});
            skLineSegment(sketch, "E79", {"start": v(94.05, 208.38) * mm, "end": v(94.05, 238.38) * mm, "construction": true});
            skCircle(sketch, "E80", {"center": v(94.05, 238.38) * mm, "radius": 6 * mm});
            skPoint(sketch, "E81.end.orphan", {"position": v(155.22, 208.38) * mm});
            skLineSegment(sketch, "E82", {"start": v(61.05, 208.38) * mm, "end": v(79.05, 226.38) * mm});
            skLineSegment(sketch, "E83", {"start": v(127.05, 208.38) * mm, "end": v(109.05, 226.38) * mm});
            skLineSegment(sketch, "E84", {"start": v(79.05, 226.38) * mm, "end": v(79.05, 238.38) * mm});
            skLineSegment(sketch, "E85", {"start": v(109.05, 226.38) * mm, "end": v(109.05, 238.38) * mm});
            skArc(sketch, "E86", {"start": v(109.05, 238.38) * mm, "mid": v(94.05, 253.38) * mm, "end": v(79.05, 238.38) * mm});
            skLineSegment(sketch, "E87", {"start": v(61.05, 208.38) * mm, "end": v(127.05, 208.38) * mm});
            skLineSegment(sketch, "E88", {"start": v(94.05, 28.38) * mm, "end": v(94.05, 208.38) * mm, "construction": true});
            skArc(sketch, "E89.MirrorCS", {"start": v(79.05, 238.38) * mm, "mid": v(94.05, 253.38) * mm, "end": v(109.05, 238.38) * mm});
            skLineSegment(sketch, "E90.MirrorCS", {"start": v(94.05, 208.38) * mm, "end": v(94.05, 238.38) * mm});
            skLineSegment(sketch, "E91.MirrorCS", {"start": v(79.05, 10.38) * mm, "end": v(79.05, -1.62) * mm});
            skLineSegment(sketch, "E92.MirrorCS", {"start": v(109.05, 10.38) * mm, "end": v(109.05, -1.62) * mm});
            skCircle(sketch, "E93.MirrorC", {"center": v(94.05, -1.62) * mm, "radius": 6 * mm});
            skLineSegment(sketch, "E94.MirrorCS", {"start": v(61.05, 28.38) * mm, "end": v(79.05, 10.38) * mm});
            skLineSegment(sketch, "E95.MirrorCS", {"start": v(127.05, 28.38) * mm, "end": v(109.05, 10.38) * mm});
            skArc(sketch, "E96.MirrorCS", {"start": v(109.05, -1.62) * mm, "mid": v(94.05, -16.62) * mm, "end": v(79.05, -1.62) * mm});
            skSolve(sketch);
        }
        {
            var Q0;
            Q0=makeQuery(id+"F16.imprint","IMPRINT",FACE,{"disambiguationData":[TD([[makeQuery(id+"F16.imprint","IMPRINT",EDGE,{"derivedFrom":sQuery(id+"F16.wireOp",EDGE,"E86")}),1.0]])]});
            var Q1;
            Q1=makeQuery(id+"F16.imprint","IMPRINT",FACE,{"disambiguationData":[TD([[makeQuery(id+"F16.imprint","IMPRINT",EDGE,{"derivedFrom":sQuery(id+"F16.wireOp",EDGE,"E91.MirrorCS")}),1.0]])]});
            var Q2;
            Q2=makeQuery(id+"F1.opExtrude","CAP_FACE",FACE,{"disambiguationData":[OSD([sQuery(id+"F0.wireOp",EDGE,"E1.bottom"),sQuery(id+"F0.wireOp",EDGE,"E1.top"),sQuery(id+"F0.wireOp",EDGE,"E1.left"),sQuery(id+"F0.wireOp",EDGE,"E1.right"),sQuery(id+"F0.wireOp",EDGE,"E4"),sQuery(id+"F0.wireOp",EDGE,"E5"),sQuery(id+"F0.wireOp",EDGE,"E6"),sQuery(id+"F0.wireOp",EDGE,"E7"),sQuery(id+"F0.wireOp",EDGE,"E21.filletArc"),sQuery(id+"F0.wireOp",EDGE,"E22.filletArc"),sQuery(id+"F0.wireOp",EDGE,"E23.filletArc"),sQuery(id+"F0.wireOp",EDGE,"E24.filletArc")])],"isStart":false});
            extrude(context, id + "F17", {"entities" : qUnion([Q0, Q1]), "operationType" : NewBodyOperationType.ADD, "endBound" : BoundingType.UP_TO_SURFACE, "oppositeDirection" : true, "endBoundEntityFace" : qUnion([Q2]), "depth" : 2 * mm});
        }
    });
